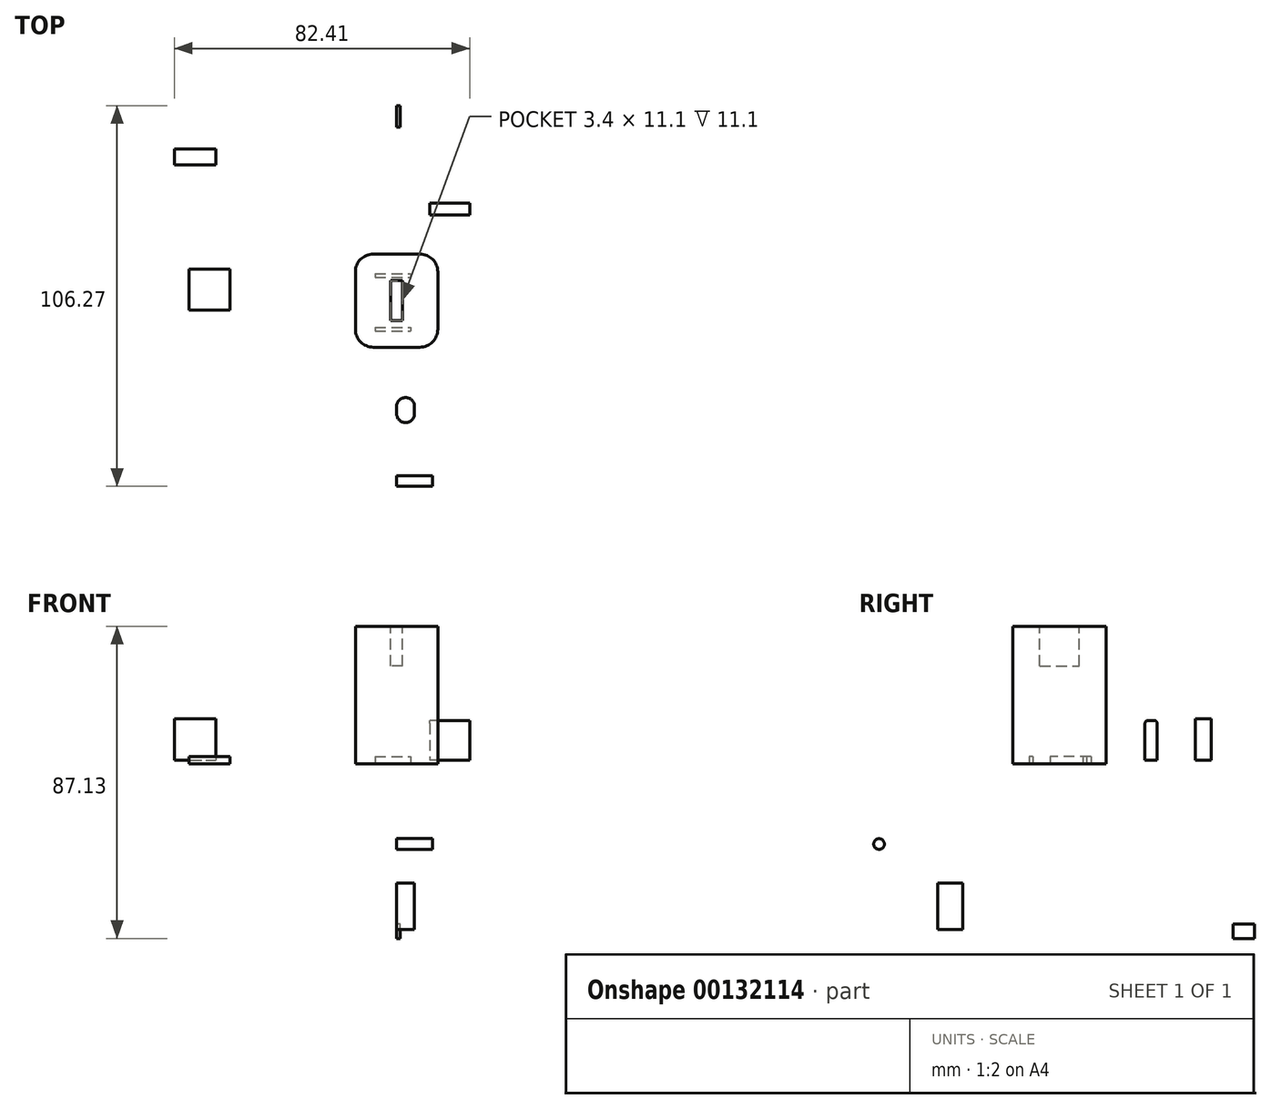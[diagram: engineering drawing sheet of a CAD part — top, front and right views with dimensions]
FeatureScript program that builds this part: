
annotation { "Feature Type Name" : "Feature", "Feature Type Description" : "" }
export const myFeature = defineFeature(function(context is Context, id is Id, definition is map)
    precondition{}
    {
        {
            var Q0;
            Q0=qCreatedBy(makeId("Top.planeOp"),FACE);
            var sketch = newSketch(context, id + "F0", { "sketchPlane" : qUnion([Q0])});
            skLineSegment(sketch, "E0.bottom", {"start": v(6.5, 13) * mm, "end": v(-6.5, 13) * mm});
            skLineSegment(sketch, "E0.top", {"start": v(6.5, -13) * mm, "end": v(-6.5, -13) * mm});
            skLineSegment(sketch, "E0.left", {"start": v(11.5, 8) * mm, "end": v(11.5, -8) * mm});
            skLineSegment(sketch, "E0.right", {"start": v(-11.5, 8) * mm, "end": v(-11.5, -8) * mm});
            skPoint(sketch, "E0.middle", {"position": v(0, 0) * mm});
            skPoint(sketch, "E1.visualSharp", {"position": v(-11.5, 13) * mm});
            skArc(sketch, "E1.filletArc", {"start": v(-6.5, 13) * mm, "mid": v(-10.04, 11.54) * mm, "end": v(-11.5, 8) * mm});
            skPoint(sketch, "E2.visualSharp", {"position": v(11.5, 13) * mm});
            skArc(sketch, "E2.filletArc", {"start": v(11.5, 8) * mm, "mid": v(10.04, 11.54) * mm, "end": v(6.5, 13) * mm});
            skPoint(sketch, "E3.visualSharp", {"position": v(11.5, -13) * mm});
            skArc(sketch, "E3.filletArc", {"start": v(6.5, -13) * mm, "mid": v(10.04, -11.54) * mm, "end": v(11.5, -8) * mm});
            skPoint(sketch, "E4.visualSharp", {"position": v(-11.5, -13) * mm});
            skArc(sketch, "E4.filletArc", {"start": v(-11.5, -8) * mm, "mid": v(-10.04, -11.54) * mm, "end": v(-6.5, -13) * mm});
            skLineSegment(sketch, "E5.bottom", {"start": v(-74.8, -30.07) * mm, "end": v(-38.76, -30.07) * mm});
            skLineSegment(sketch, "E5.top", {"start": v(-74.8, -65.15) * mm, "end": v(-38.76, -65.15) * mm});
            skLineSegment(sketch, "E5.left", {"start": v(-74.8, -30.07) * mm, "end": v(-74.8, -65.15) * mm});
            skPoint(sketch, "E6.end.orphan", {"position": v(-55.44, -42.51) * mm});
            skPoint(sketch, "E7.end.orphan", {"position": v(-38.94, -42.51) * mm});
            skPoint(sketch, "E8.center.orphan", {"position": v(-58.48, -47.51) * mm});
            skPoint(sketch, "E9.end.orphan", {"position": v(-63.04, -45.01) * mm});
            skPoint(sketch, "E10.end.orphan", {"position": v(-63.04, -50.01) * mm});
            skPoint(sketch, "E11.end.orphan", {"position": v(-38.94, -52.51) * mm});
            skPoint(sketch, "E11.start.orphan", {"position": v(-55.44, -52.51) * mm});
            skLineSegment(sketch, "E12.bottom", {"start": v(-57.85, 8.77) * mm, "end": v(-46.45, 8.77) * mm});
            skLineSegment(sketch, "E12.top", {"start": v(-57.85, -2.63) * mm, "end": v(-46.45, -2.63) * mm});
            skLineSegment(sketch, "E12.left", {"start": v(-57.85, 8.77) * mm, "end": v(-57.85, -2.63) * mm});
            skLineSegment(sketch, "E12.right", {"start": v(-46.45, 8.77) * mm, "end": v(-46.45, -2.63) * mm});
            skSolve(sketch);
        }
        {
            var Q0;
            Q0=makeQuery(id+"F0.imprint","IMPRINT",FACE,{"disambiguationData":[TD([[makeQuery(id+"F0.imprint","IMPRINT",EDGE,{"derivedFrom":sQuery(id+"F0.wireOp",EDGE,"E0.bottom")}),1.0]])]});
            extrude(context, id + "F1", {"entities" : qUnion([Q0]), "depth" : 37.4 * mm});
        }
        {
            var Q0;
            Q0 = qSketchRegion(id + "F0", true);
            extrude(context, id + "F2", {"entities" : qUnion([Q0]), "operationType" : NewBodyOperationType.ADD, "depth" : 1 * mm, "hasSecondDirection" : true, "secondDirectionOppositeDirection" : true, "secondDirectionDepth" : 1 * mm});
        }
        {
            var Q0;
            Q0=qCreatedBy(makeId("Front.planeOp"),FACE);
            cPlane(context, id + "F3", {"entities" : qUnion([Q0]), "cplaneType" : CPlaneType.OFFSET, "offset" : 10 * mm, "width" : 150 * mm, "height" : 150 * mm});
        }
        {
            var Q0;
            Q0=qCreatedBy(makeId("Top.planeOp"),FACE);
            var sketch = newSketch(context, id + "F4", { "sketchPlane" : qUnion([Q0])});
            skLineSegment(sketch, "E13.bottom", {"start": v(20.4, 23.86) * mm, "end": v(9.3, 23.86) * mm});
            skLineSegment(sketch, "E13.top", {"start": v(20.4, 27.26) * mm, "end": v(9.3, 27.26) * mm});
            skLineSegment(sketch, "E13.left", {"start": v(20.4, 23.86) * mm, "end": v(20.4, 27.26) * mm});
            skLineSegment(sketch, "E13.right", {"start": v(9.3, 23.86) * mm, "end": v(9.3, 27.26) * mm});
            skPoint(sketch, "E13.middle", {"position": v(14.86, 25.56) * mm});
            skSolve(sketch);
        }
        {
            var Q0;
            Q0=makeQuery(id+"F4.imprint","IMPRINT",FACE,{"disambiguationData":[TD([[makeQuery(id+"F4.imprint","IMPRINT",EDGE,{"derivedFrom":sQuery(id+"F4.wireOp",EDGE,"E13.bottom")}),-1.0]])]});
            extrude(context, id + "F5", {"entities" : qUnion([Q0]), "depth" : 11.1 * mm});
        }
        {
            var Q0;
            Q0=qCreatedBy(makeId("Top.planeOp"),FACE);
            var sketch = newSketch(context, id + "F6", { "sketchPlane" : qUnion([Q0])});
            skLineSegment(sketch, "E14.bottom", {"start": v(-62, 42.3) * mm, "end": v(-50.4, 42.3) * mm});
            skLineSegment(sketch, "E14.top", {"start": v(-62, 37.9) * mm, "end": v(-50.4, 37.9) * mm});
            skLineSegment(sketch, "E14.left", {"start": v(-62, 42.3) * mm, "end": v(-62, 37.9) * mm});
            skLineSegment(sketch, "E14.right", {"start": v(-50.4, 42.3) * mm, "end": v(-50.4, 37.9) * mm});
            skSolve(sketch);
        }
        {
            var Q0;
            Q0 = qSketchRegion(id + "F6", true);
            extrude(context, id + "F7", {"entities" : qUnion([Q0]), "depth" : 11.6 * mm});
        }
        {
            var Q0;
            Q0=qCreatedBy(makeId("Right.planeOp"),FACE);
            var sketch = newSketch(context, id + "F8", { "sketchPlane" : qUnion([Q0])});
            skCircle(sketch, "E15", {"center": v(-50.35, -23.39) * mm, "radius": 1.5 * mm});
            skSolve(sketch);
        }
        {
            var Q0;
            Q0 = qSketchRegion(id + "F8", true);
            extrude(context, id + "F9", {"entities" : qUnion([Q0]), "depth" : 10 * mm});
        }
        {
            var Q0;
            Q0=qCreatedBy(makeId("Right.planeOp"),FACE);
            var sketch = newSketch(context, id + "F10", { "sketchPlane" : qUnion([Q0])});
            skLineSegment(sketch, "E16.bottom", {"start": v(54.42, -49.73) * mm, "end": v(48.42, -49.73) * mm});
            skLineSegment(sketch, "E16.top", {"start": v(54.42, -45.73) * mm, "end": v(48.42, -45.73) * mm});
            skLineSegment(sketch, "E16.left", {"start": v(54.42, -49.73) * mm, "end": v(54.42, -45.73) * mm});
            skLineSegment(sketch, "E16.right", {"start": v(48.42, -49.73) * mm, "end": v(48.42, -45.73) * mm});
            skPoint(sketch, "E16.middle", {"position": v(51.42, -47.73) * mm});
            skSolve(sketch);
        }
        {
            var Q0;
            Q0=makeQuery(id+"F10.imprint","IMPRINT",FACE,{"disambiguationData":[TD([[makeQuery(id+"F10.imprint","IMPRINT",EDGE,{"derivedFrom":sQuery(id+"F10.wireOp",EDGE,"E16.bottom")}),-1.0]])]});
            extrude(context, id + "F11", {"entities" : qUnion([Q0]), "depth" : 1 * mm});
        }
        {
            var Q0;
            Q0=qCreatedBy(makeId("Right.planeOp"),FACE);
            var sketch = newSketch(context, id + "F12", { "sketchPlane" : qUnion([Q0])});
            skLineSegment(sketch, "E17.bottom", {"start": v(-34.05, -34.27) * mm, "end": v(-27.05, -34.27) * mm});
            skLineSegment(sketch, "E17.top", {"start": v(-34.05, -47.27) * mm, "end": v(-27.05, -47.27) * mm});
            skLineSegment(sketch, "E17.left", {"start": v(-34.05, -34.27) * mm, "end": v(-34.05, -47.27) * mm});
            skLineSegment(sketch, "E17.right", {"start": v(-27.05, -34.27) * mm, "end": v(-27.05, -47.27) * mm});
            skSolve(sketch);
        }
        {
            var Q0;
            Q0=makeQuery(id+"F12.imprint","IMPRINT",FACE,{"disambiguationData":[TD([[makeQuery(id+"F12.imprint","IMPRINT",EDGE,{"derivedFrom":sQuery(id+"F12.wireOp",EDGE,"E17.bottom")}),-1.0]])]});
            extrude(context, id + "F13", {"entities" : qUnion([Q0]), "depth" : 5 * mm});
        }
        {
            var Q0;
            Q0=makeQuery(id+"F13.opExtrude","CAP_EDGE",EDGE,{"disambiguationData":[OSD([sQuery(id+"F12.wireOp",EDGE,"E17.left")])],"isStart":false});
            var Q1;
            Q1=makeQuery(id+"F13.opExtrude","CAP_EDGE",EDGE,{"disambiguationData":[OSD([sQuery(id+"F12.wireOp",EDGE,"E17.right")])],"isStart":false});
            var Q2;
            Q2=makeQuery(id+"F13.opExtrude","CAP_EDGE",EDGE,{"disambiguationData":[OSD([sQuery(id+"F12.wireOp",EDGE,"E17.right")])],"isStart":true});
            var Q3;
            Q3=makeQuery(id+"F13.opExtrude","CAP_EDGE",EDGE,{"disambiguationData":[OSD([sQuery(id+"F12.wireOp",EDGE,"E17.left")])],"isStart":true});
            fillet(context, id + "F14", {"entities" : qUnion([Q0, Q1, Q2, Q3]), "radius" : 2.5 * mm, "tangentPropagation" : true, "allowEdgeOverflow" : false});
        }
        {
            var Q0;
            Q0=makeQuery(id+"F1.opExtrude","CAP_FACE",FACE,{"disambiguationData":[OSD([sQuery(id+"F0.wireOp",EDGE,"E0.bottom"),sQuery(id+"F0.wireOp",EDGE,"E0.top"),sQuery(id+"F0.wireOp",EDGE,"E0.left"),sQuery(id+"F0.wireOp",EDGE,"E0.right"),sQuery(id+"F0.wireOp",EDGE,"E1.filletArc"),sQuery(id+"F0.wireOp",EDGE,"E2.filletArc"),sQuery(id+"F0.wireOp",EDGE,"E3.filletArc"),sQuery(id+"F0.wireOp",EDGE,"E4.filletArc")])],"isStart":false});
            var sketch = newSketch(context, id + "F15", { "sketchPlane" : qUnion([Q0])});
            skLineSegment(sketch, "E18.bottom", {"start": v(1.7, -5.55) * mm, "end": v(-1.7, -5.55) * mm});
            skLineSegment(sketch, "E18.top", {"start": v(1.7, 5.55) * mm, "end": v(-1.7, 5.55) * mm});
            skLineSegment(sketch, "E18.left", {"start": v(1.7, -5.55) * mm, "end": v(1.7, 5.55) * mm});
            skLineSegment(sketch, "E18.right", {"start": v(-1.7, -5.55) * mm, "end": v(-1.7, 5.55) * mm});
            skPoint(sketch, "E18.middle", {"position": v(0, 0) * mm});
            skSolve(sketch);
        }
        {
            var Q0;
            Q0 = qSketchRegion(id + "F15", true);
            extrude(context, id + "F16", {"entities" : qUnion([Q0]), "operationType" : NewBodyOperationType.REMOVE, "oppositeDirection" : true, "depth" : 11.1 * mm});
        }
        {
            var Q0;
            Q0=makeQuery(id+"F5.opExtrude","CAP_EDGE",EDGE,{"disambiguationData":[OSD([sQuery(id+"F4.wireOp",EDGE,"E13.top")])],"isStart":false});
            var Q1;
            Q1=makeQuery(id+"F5.opExtrude","CAP_EDGE",EDGE,{"disambiguationData":[OSD([sQuery(id+"F4.wireOp",EDGE,"E13.bottom")])],"isStart":false});
            fillet(context, id + "F17", {"entities" : qUnion([Q0, Q1]), "radius" : 0.85 * mm, "allowEdgeOverflow" : false});
        }
        {
            var Q0;
            Q0=makeQuery(id+"F2.opExtrude","CAP_FACE",FACE,{"disambiguationData":[OSD([sQuery(id+"F0.wireOp",EDGE,"E0.bottom"),sQuery(id+"F0.wireOp",EDGE,"E0.top"),sQuery(id+"F0.wireOp",EDGE,"E0.left"),sQuery(id+"F0.wireOp",EDGE,"E0.right"),sQuery(id+"F0.wireOp",EDGE,"E1.filletArc"),sQuery(id+"F0.wireOp",EDGE,"E2.filletArc"),sQuery(id+"F0.wireOp",EDGE,"E3.filletArc"),sQuery(id+"F0.wireOp",EDGE,"E4.filletArc")])],"isStart":true});
            var sketch = newSketch(context, id + "F18", { "sketchPlane" : qUnion([Q0])});
            skLineSegment(sketch, "E19.bottom", {"start": v(-6, -7.5) * mm, "end": v(4, -7.5) * mm});
            skLineSegment(sketch, "E19.top", {"start": v(-6, -6.5) * mm, "end": v(4, -6.5) * mm});
            skLineSegment(sketch, "E19.left", {"start": v(-6, -7.5) * mm, "end": v(-6, -6.5) * mm});
            skLineSegment(sketch, "E19.right", {"start": v(4, -7.5) * mm, "end": v(4, -6.5) * mm});
            skLineSegment(sketch, "E20.bottom", {"start": v(-6, 7.5) * mm, "end": v(4, 7.5) * mm});
            skLineSegment(sketch, "E20.top", {"start": v(-6, 8.5) * mm, "end": v(4, 8.5) * mm});
            skLineSegment(sketch, "E20.left", {"start": v(-6, 7.5) * mm, "end": v(-6, 8.5) * mm});
            skLineSegment(sketch, "E20.right", {"start": v(4, 7.5) * mm, "end": v(4, 8.5) * mm});
            skSolve(sketch);
        }
        {
            var Q0;
            Q0 = qSketchRegion(id + "F18", true);
            extrude(context, id + "F19", {"entities" : qUnion([Q0]), "operationType" : NewBodyOperationType.REMOVE, "oppositeDirection" : true, "depth" : 2 * mm});
        }
    });
